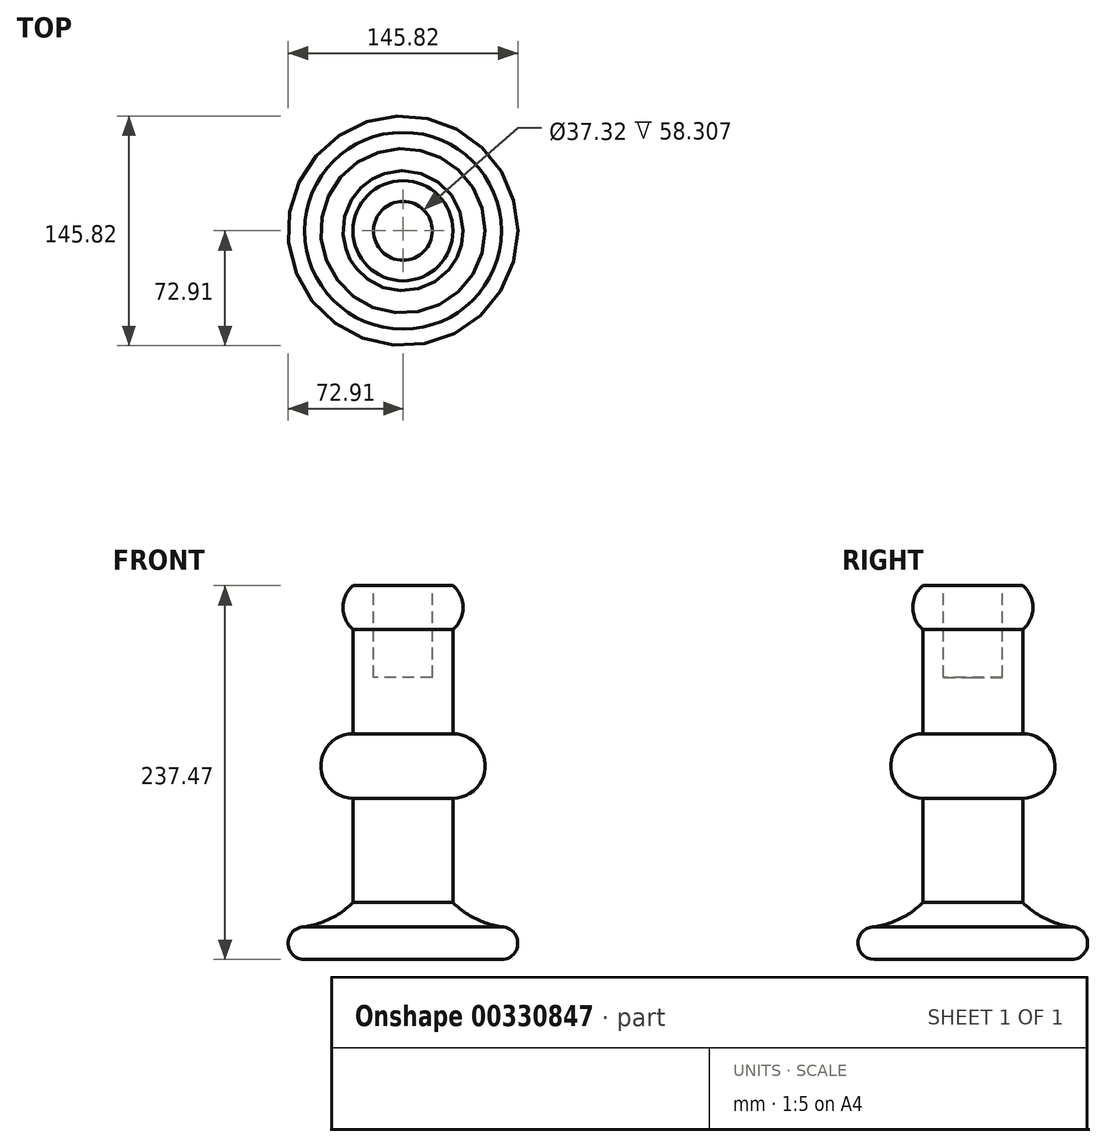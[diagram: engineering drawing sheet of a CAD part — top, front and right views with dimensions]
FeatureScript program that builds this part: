
annotation { "Feature Type Name" : "Feature", "Feature Type Description" : "" }
export const myFeature = defineFeature(function(context is Context, id is Id, definition is map)
    precondition{}
    {
        {
            var Q0;
            Q0=qCreatedBy(makeId("Front.planeOp"),FACE);
            var sketch = newSketch(context, id + "F0", { "sketchPlane" : qUnion([Q0])});
            skLineSegment(sketch, "E0", {"start": v(0, 0) * mm, "end": v(62.52, 0) * mm});
            skArc(sketch, "E1", {"start": v(62.52, 0) * mm, "mid": v(72.91, 10.4) * mm, "end": v(62.52, 20.79) * mm});
            skArc(sketch, "E2", {"start": v(31.8, 36.18) * mm, "mid": v(45.91, 26) * mm, "end": v(62.52, 20.79) * mm});
            skLineSegment(sketch, "E3", {"start": v(31.8, 36.18) * mm, "end": v(31.8, 102.48) * mm});
            skArc(sketch, "E4", {"start": v(31.8, 209.63) * mm, "mid": v(38.14, 223.55) * mm, "end": v(31.8, 237.47) * mm});
            skLineSegment(sketch, "E5", {"start": v(31.8, 237.47) * mm, "end": v(18.66, 237.47) * mm});
            skLineSegment(sketch, "E6", {"start": v(18.66, 237.47) * mm, "end": v(18.66, 179.16) * mm});
            skLineSegment(sketch, "E7", {"start": v(18.66, 179.16) * mm, "end": v(0, 179.16) * mm});
            skLineSegment(sketch, "E8", {"start": v(0, 179.16) * mm, "end": v(0, 0) * mm});
            skArc(sketch, "E9", {"start": v(31.8, 102.48) * mm, "mid": v(52.21, 122.9) * mm, "end": v(31.8, 143.33) * mm});
            skLineSegment(sketch, "E10.trimOffspring", {"start": v(31.8, 143.33) * mm, "end": v(31.8, 209.63) * mm});
            skSolve(sketch);
        }
        {
            var Q0;
            Q0=makeQuery(id+"F0.imprint","IMPRINT",FACE,{"disambiguationData":[TD([[makeQuery(id+"F0.imprint","IMPRINT",EDGE,{"derivedFrom":sQuery(id+"F0.wireOp",EDGE,"E0")}),1.0]])]});
            var Q1;
            Q1=sQuery(id+"F0.wireOp",EDGE,"E8");
            revolve(context, id + "F1", {"entities" : qUnion([Q0]), "axis" : qUnion([Q1]), "revolveType" : RevolveType.FULL});
        }
    });
